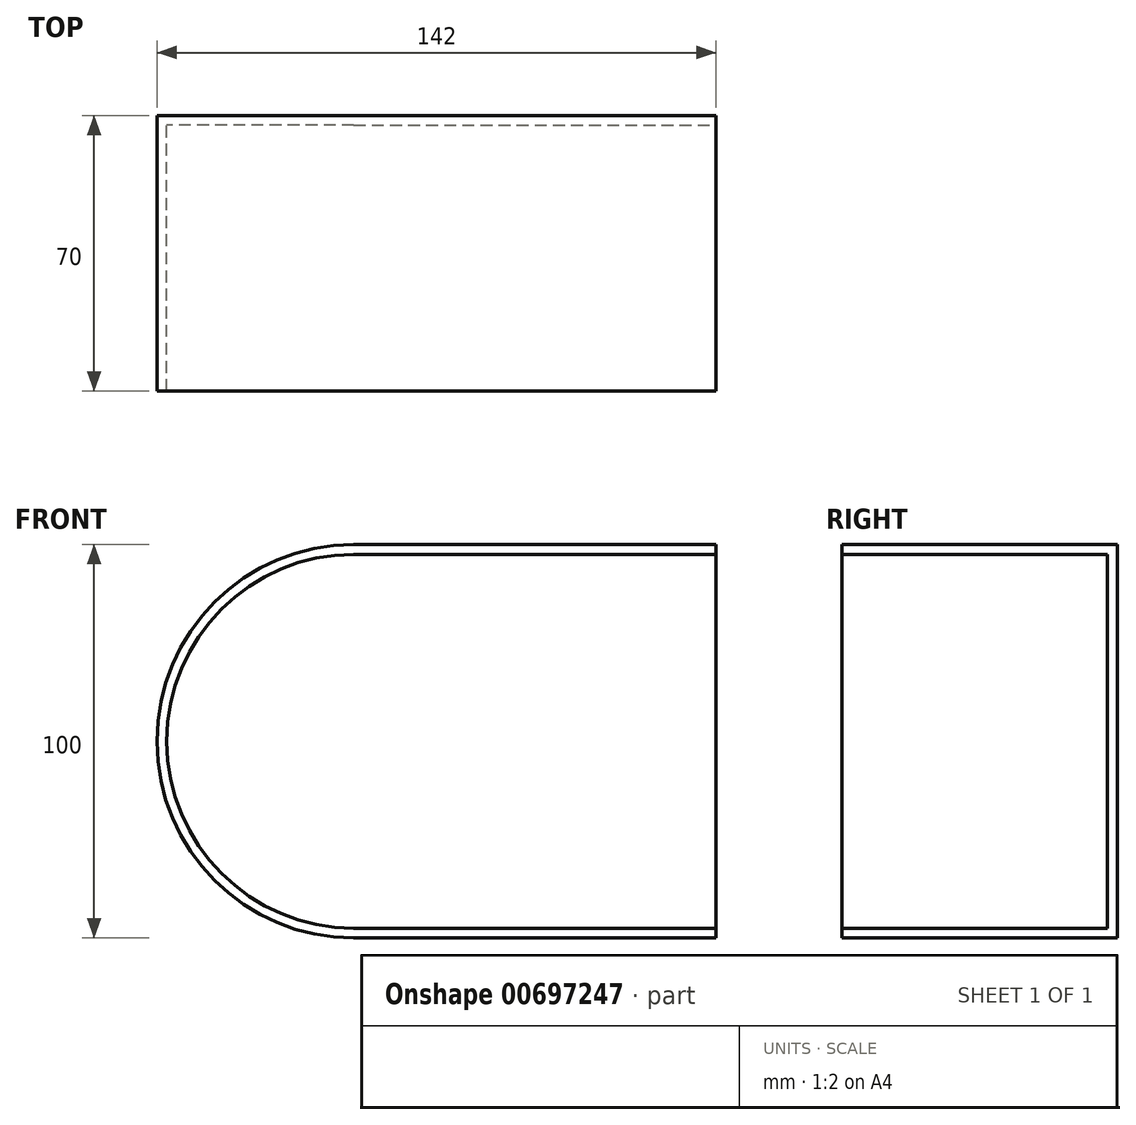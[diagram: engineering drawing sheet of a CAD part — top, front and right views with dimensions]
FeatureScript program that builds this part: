
annotation { "Feature Type Name" : "Feature", "Feature Type Description" : "" }
export const myFeature = defineFeature(function(context is Context, id is Id, definition is map)
    precondition{}
    {
        {
            var Q0;
            Q0=qCreatedBy(makeId("Front.planeOp"),FACE);
            var sketch = newSketch(context, id + "F0", { "sketchPlane" : qUnion([Q0])});
            skArc(sketch, "E0", {"start": v(-126.64, 57.97) * mm, "mid": v(-176.64, 7.97) * mm, "end": v(-126.64, -42.03) * mm});
            skLineSegment(sketch, "E1", {"start": v(-126.64, 57.97) * mm, "end": v(-34.64, 57.97) * mm});
            skLineSegment(sketch, "E2", {"start": v(-126.64, -42.03) * mm, "end": v(-34.64, -42.03) * mm});
            skLineSegment(sketch, "E3", {"start": v(-34.64, -42.03) * mm, "end": v(-34.64, 57.97) * mm});
            skPoint(sketch, "E4.end.orphan", {"position": v(-176.64, 7.97) * mm});
            skSolve(sketch);
        }
        {
            var Q0;
            Q0 = qSketchRegion(id + "F0", true);
            extrude(context, id + "F1", {"entities" : qUnion([Q0]), "depth" : 70 * mm, "offsetDistance" : 25 * mm});
        }
        {
            var Q0;
            Q0=makeQuery(id+"F1.opExtrude","SWEPT_FACE",FACE,{"disambiguationData":[OSD([sQuery(id+"F0.wireOp",EDGE,"E3")])]});
            var Q1;
            Q1=makeQuery(id+"F1.opExtrude","CAP_FACE",FACE,{"disambiguationData":[OSD([sQuery(id+"F0.wireOp",EDGE,"E0"),sQuery(id+"F0.wireOp",EDGE,"E1"),sQuery(id+"F0.wireOp",EDGE,"E2"),sQuery(id+"F0.wireOp",EDGE,"E3")])],"isStart":false});
            shell(context, id + "F2", {"entities" : qUnion([Q0, Q1]), "thickness" : 2.5 * mm});
        }
    });
